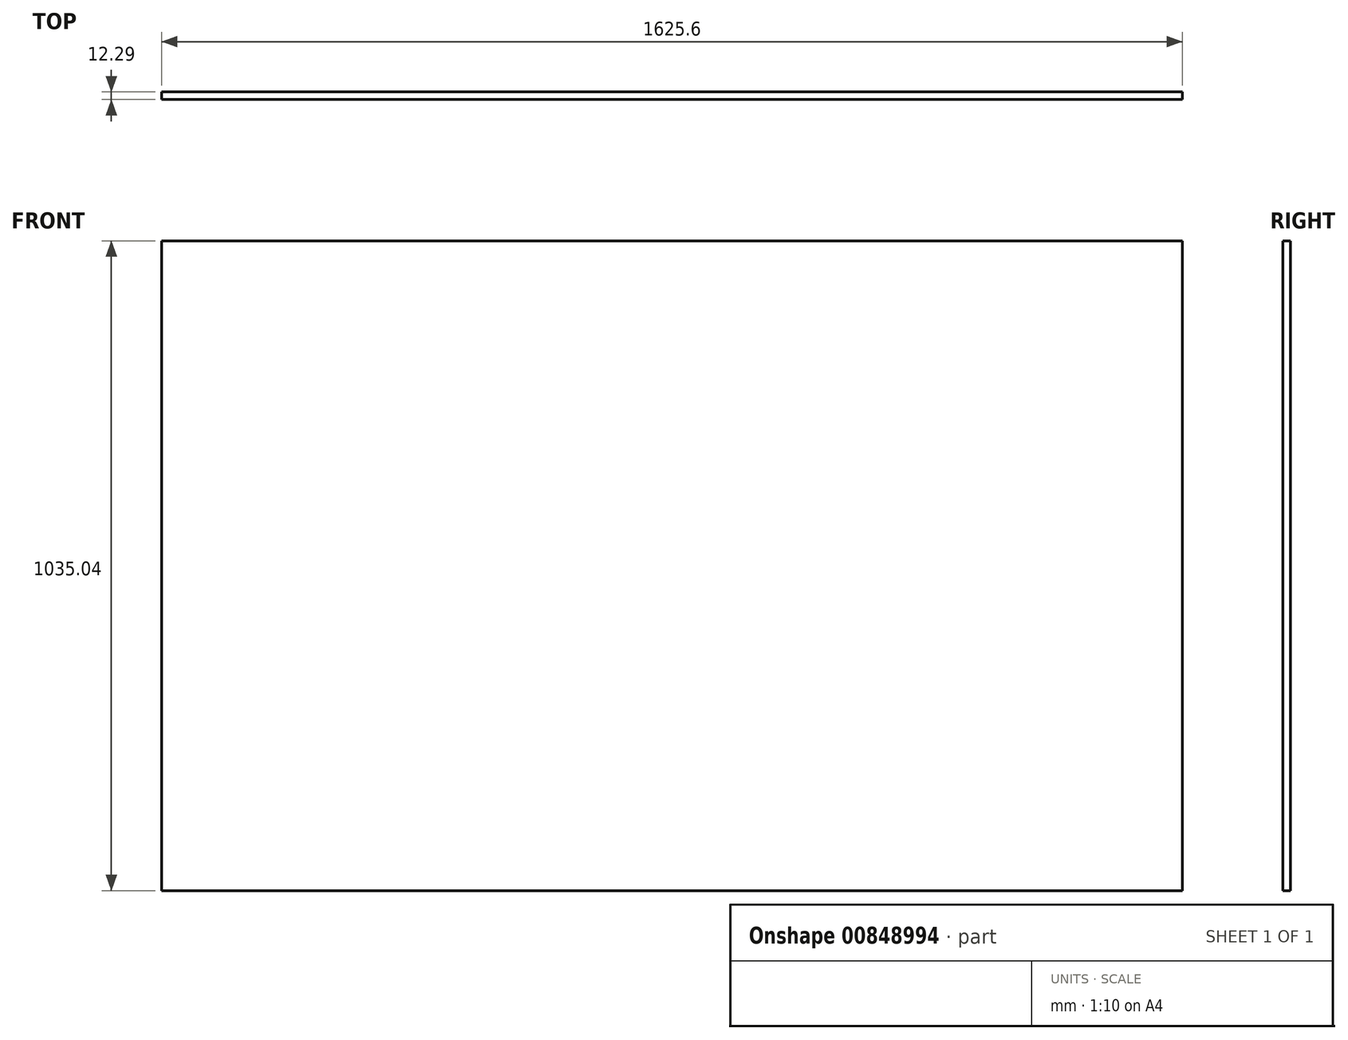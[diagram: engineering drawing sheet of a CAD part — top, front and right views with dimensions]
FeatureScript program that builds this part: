
annotation { "Feature Type Name" : "Feature", "Feature Type Description" : "" }
export const myFeature = defineFeature(function(context is Context, id is Id, definition is map)
    precondition{}
    {
        {
            var Q0;
            Q0=qCreatedBy(makeId("Front.planeOp"),FACE);
            var sketch = newSketch(context, id + "F0", { "sketchPlane" : qUnion([Q0])});
            skLineSegment(sketch, "E0.bottom", {"start": v(812.8, -517.52) * mm, "end": v(-812.8, -517.52) * mm});
            skLineSegment(sketch, "E0.top", {"start": v(812.8, 517.53) * mm, "end": v(-812.8, 517.52) * mm});
            skLineSegment(sketch, "E0.left", {"start": v(812.8, -517.52) * mm, "end": v(812.8, 517.52) * mm});
            skLineSegment(sketch, "E0.right", {"start": v(-812.8, -517.52) * mm, "end": v(-812.8, 517.52) * mm});
            skPoint(sketch, "E0.middle", {"position": v(0, 0) * mm});
            skSolve(sketch);
        }
        {
            var Q0;
            Q0=makeQuery(id+"F0.imprint","IMPRINT",FACE,{"disambiguationData":[TD([[makeQuery(id+"F0.imprint","IMPRINT",EDGE,{"derivedFrom":sQuery(id+"F0.wireOp",EDGE,"E0.bottom")}),-1.0]])]});
            extrude(context, id + "F1", {"entities" : qUnion([Q0]), "depth" : 12.3 * mm, "offsetDistance" : 25.4 * mm});
        }
    });
